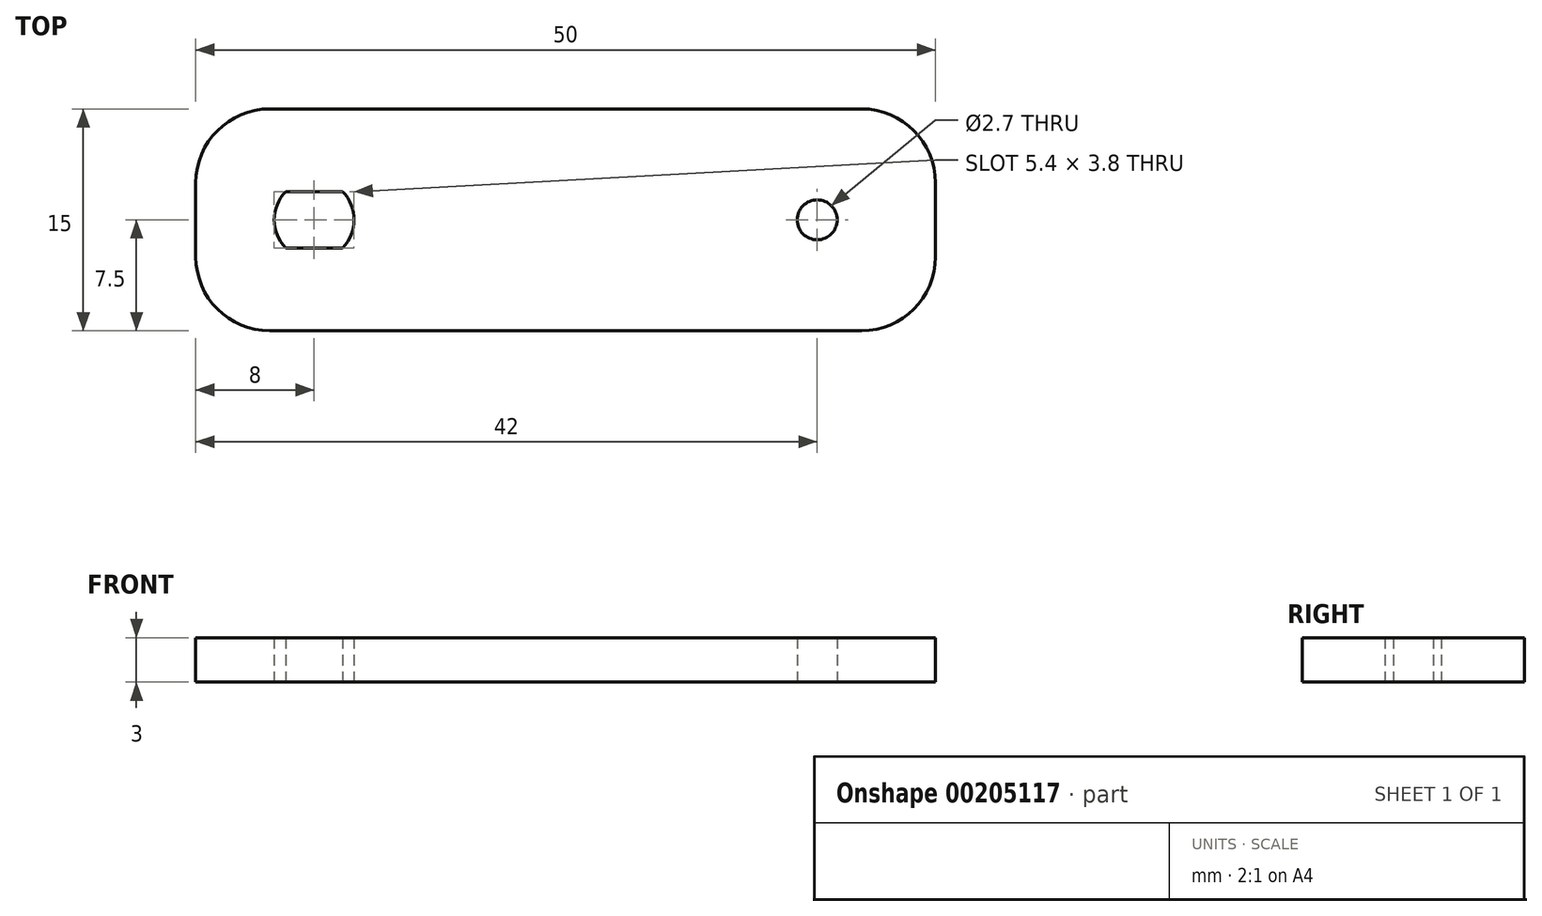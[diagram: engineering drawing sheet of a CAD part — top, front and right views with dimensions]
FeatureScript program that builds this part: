
annotation { "Feature Type Name" : "Feature", "Feature Type Description" : "" }
export const myFeature = defineFeature(function(context is Context, id is Id, definition is map)
    precondition{}
    {
        {
            var Q0;
            Q0=qCreatedBy(makeId("Top.planeOp"),FACE);
            var sketch = newSketch(context, id + "F0", { "sketchPlane" : qUnion([Q0])});
            skLineSegment(sketch, "E0.bottom", {"start": v(5, 0) * mm, "end": v(45, 0) * mm});
            skLineSegment(sketch, "E0.top", {"start": v(5, -15) * mm, "end": v(45, -15) * mm});
            skLineSegment(sketch, "E0.left", {"start": v(0, -5) * mm, "end": v(0, -10) * mm});
            skLineSegment(sketch, "E0.right", {"start": v(50, -5) * mm, "end": v(50, -10) * mm});
            skPoint(sketch, "E1.visualSharp", {"position": v(0, 0) * mm});
            skArc(sketch, "E1.filletArc", {"start": v(5, 0) * mm, "mid": v(1.46, -1.46) * mm, "end": v(0, -5) * mm});
            skPoint(sketch, "E2.visualSharp", {"position": v(50, 0) * mm});
            skArc(sketch, "E2.filletArc", {"start": v(50, -5) * mm, "mid": v(48.54, -1.46) * mm, "end": v(45, 0) * mm});
            skPoint(sketch, "E3.visualSharp", {"position": v(0, -15) * mm});
            skArc(sketch, "E3.filletArc", {"start": v(0, -10) * mm, "mid": v(1.46, -13.54) * mm, "end": v(5, -15) * mm});
            skPoint(sketch, "E4.visualSharp", {"position": v(50, -15) * mm});
            skArc(sketch, "E4.filletArc", {"start": v(45, -15) * mm, "mid": v(48.54, -13.54) * mm, "end": v(50, -10) * mm});
            skLineSegment(sketch, "E5", {"start": v(0, -7.5) * mm, "end": v(50, -7.5) * mm});
            skArc(sketch, "E6", {"start": v(6.08, -5.6) * mm, "mid": v(5.3, -7.5) * mm, "end": v(6.08, -9.4) * mm});
            skLineSegment(sketch, "E7", {"start": v(6.08, -5.6) * mm, "end": v(9.92, -5.6) * mm});
            skLineSegment(sketch, "E8", {"start": v(6.08, -9.4) * mm, "end": v(9.92, -9.4) * mm});
            skArc(sketch, "E9.trimOffspring", {"start": v(9.92, -9.4) * mm, "mid": v(10.7, -7.5) * mm, "end": v(9.92, -5.6) * mm});
            skCircle(sketch, "E10", {"center": v(42, -7.5) * mm, "radius": 1.35 * mm});
            skSolve(sketch);
        }
        {
            var Q0;
            Q0 = qSketchRegion(id + "F0", true);
            extrude(context, id + "F1", {"entities" : qUnion([Q0]), "depth" : 3 * mm});
        }
    });
